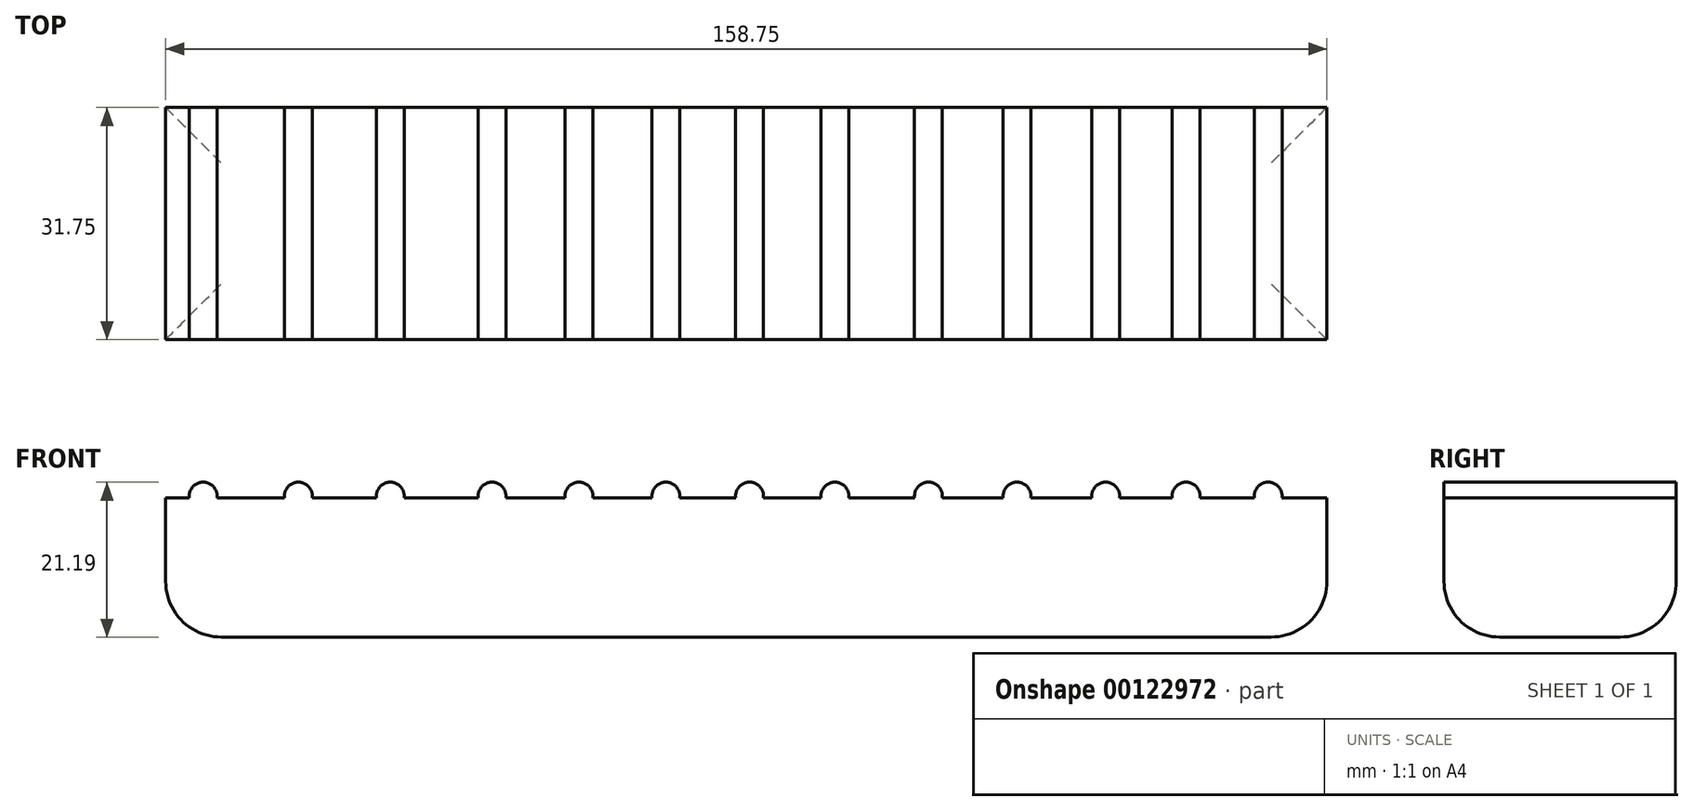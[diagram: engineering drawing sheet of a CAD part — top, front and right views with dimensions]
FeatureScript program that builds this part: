
annotation { "Feature Type Name" : "Feature", "Feature Type Description" : "" }
export const myFeature = defineFeature(function(context is Context, id is Id, definition is map)
    precondition{}
    {
        {
            var Q0;
            Q0=qCreatedBy(makeId("Top.planeOp"),FACE);
            var sketch = newSketch(context, id + "F0", { "sketchPlane" : qUnion([Q0])});
            skLineSegment(sketch, "E0", {"start": v(-123.25, 22) * mm, "end": v(-123.25, -9.75) * mm});
            skLineSegment(sketch, "E1", {"start": v(-123.25, -9.75) * mm, "end": v(35.5, -9.75) * mm});
            skLineSegment(sketch, "E2", {"start": v(35.5, -9.75) * mm, "end": v(35.5, 22) * mm});
            skLineSegment(sketch, "E3", {"start": v(35.5, 22) * mm, "end": v(-123.25, 22) * mm});
            skSolve(sketch);
        }
        {
            var Q0;
            Q0 = qSketchRegion(id + "F0", true);
            extrude(context, id + "F1", {"entities" : qUnion([Q0]), "depth" : 19.05 * mm});
        }
        {
            var Q0;
            Q0=qCreatedBy(makeId("Front.planeOp"),FACE);
            var sketch = newSketch(context, id + "F2", { "sketchPlane" : qUnion([Q0])});
            skCircle(sketch, "E4", {"center": v(-105.11, 19.29) * mm, "radius": 1.9 * mm});
            skCircle(sketch, "E5", {"center": v(-92.55, 19.29) * mm, "radius": 1.9 * mm});
            skCircle(sketch, "E6", {"center": v(-78.64, 19.29) * mm, "radius": 1.9 * mm});
            skCircle(sketch, "E7", {"center": v(-66.75, 19.29) * mm, "radius": 1.9 * mm});
            skCircle(sketch, "E8", {"center": v(-54.86, 19.29) * mm, "radius": 1.9 * mm});
            skCircle(sketch, "E9", {"center": v(-43.42, 19.29) * mm, "radius": 1.9 * mm});
            skCircle(sketch, "E10", {"center": v(-31.76, 19.29) * mm, "radius": 1.9 * mm});
            skCircle(sketch, "E11", {"center": v(-18.97, 19.29) * mm, "radius": 1.9 * mm});
            skCircle(sketch, "E12", {"center": v(-6.86, 19.29) * mm, "radius": 1.9 * mm});
            skCircle(sketch, "E13", {"center": v(-118.12, 19.29) * mm, "radius": 1.9 * mm});
            skCircle(sketch, "E14", {"center": v(5.26, 19.29) * mm, "radius": 1.9 * mm});
            skCircle(sketch, "E15", {"center": v(16.25, 19.29) * mm, "radius": 1.9 * mm});
            skCircle(sketch, "E16", {"center": v(27.46, 19.29) * mm, "radius": 1.9 * mm});
            skSolve(sketch);
        }
        {
            var Q0;
            Q0=makeQuery(id+"F1.opExtrude","CAP_FACE",FACE,{"disambiguationData":[OSD([sQuery(id+"F0.wireOp",EDGE,"E0"),sQuery(id+"F0.wireOp",EDGE,"E1"),sQuery(id+"F0.wireOp",EDGE,"E2"),sQuery(id+"F0.wireOp",EDGE,"E3")])],"isStart":true});
            fillet(context, id + "F3", {"entities" : qUnion([Q0]), "radius" : 7.62 * mm, "tangentPropagation" : true, "allowEdgeOverflow" : false});
        }
        {
            var Q0;
            Q0 = qSketchRegion(id + "F2", true);
            var Q1;
            Q1=makeQuery(id+"F1.opExtrude","SWEPT_FACE",FACE,{"disambiguationData":[OSD([sQuery(id+"F0.wireOp",EDGE,"E3")])]});
            var Q2;
            Q2=makeQuery(id+"F1.opExtrude","SWEPT_FACE",FACE,{"disambiguationData":[OSD([sQuery(id+"F0.wireOp",EDGE,"E1")])]});
            extrude(context, id + "F4", {"entities" : qUnion([Q0]), "operationType" : NewBodyOperationType.ADD, "endBound" : BoundingType.UP_TO_SURFACE, "oppositeDirection" : true, "endBoundEntityFace" : qUnion([Q1]), "depth" : 25.4 * mm, "hasSecondDirection" : true, "secondDirectionBound" : SecondDirectionBoundingType.UP_TO_SURFACE, "secondDirectionOppositeDirection" : false, "secondDirectionBoundEntityFace" : qUnion([Q2]), "secondDirectionDepth" : 25.4 * mm});
        }
    });
